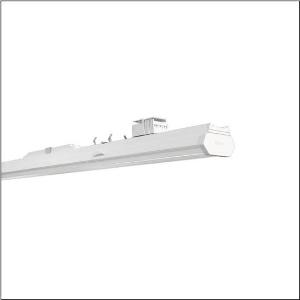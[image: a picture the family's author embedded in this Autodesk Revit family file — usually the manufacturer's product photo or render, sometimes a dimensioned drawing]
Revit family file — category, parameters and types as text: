
# Revit family: licross_r__21_protected_mo_52td1bvn48xg_aeae
name_source: partatom
category: Lighting Fixtures
units: mm (PartAtom-declared; Revit-internal decimal feet)

## family parameters
Cut with Voids When Loaded = No
Host = Face
Light Source = No
Part Type = Normal
Room Calculation Point = No
Round Connector Dimension = Use Diameter
Shared = No

## types (1)
- --- (1 x LED, 8000 lm, 48.3 W, 4000K)
    Apparent Load = 48 VA
    CIE Flux Codes = 54 82 95 97 100
    Color Rendering = 80
    Color Temperature = 4000K
    Default Elevation = 1800 mm
    Description = Licross® 21 Protected MO, luminaire insert, of sheet steel, galvanised, coil coated, white, length: 1.500mm, width: 90mm, height: 101mm, LED rated luminous flux: 8.000lm, light colour: 840, control gear: DALI 2, CLO, with plug, 5-pole, with phase selection, mains connection: 220..240V, AC, 50/60Hz, start of lifetime: 48W, end of service life: 58W, halogen-free wiring, primary optical cover: cover, of PMMA, light emission: direct distribution, primary light characteristic: symmetric, protection rating (complete): IP54, insulation class (complete): insulation class I (protective earthing), certification: CE, ENEC, VDE, UKCA, protection symbol: D if used in an environment with non-conductive dust loads with corresponding accessories, impact resistance: IK06, permissible ambient temperature for indoor applications: -25..+40°C, corresponds to IFS (International Featured Standards) requirements for safety and quality in the food industry, reducing of maximum allowable ambient temperature of 5°C with ceiling mounting, LABS conformity tested according to VDMA 24364:2018-05, packaging unit: 1 piece
    Height = 92 mm
    Lamp = 1 x LED
    Lamp Light Flux = 8000 lm
    Lamp Power = 48.3 W
    Lamp count = 1
    Length = 1500 mm
    Luminous efficacy = 166 lm/W
    Manufacturer = Siteco
    ModVariant = No
    Model = 52TD1BVN48XG
    Mounting Place = Ceiling
    Mounting Type = Pendant
    Number of Poles = 1
    OnlyDefault = Yes
    Power Factor = 1
    Product Name = Licross® 21 Protected MO
    Product group = luminaire insert
    ProductGroupID = 901
    Protection Class = Protection class I
    Protection Degree = IP 54
    RLX_Detail_Level = 1
    RLX_Emergency_Light_Flux = 0 lm
    RLX_Emergency_Type = 0
    RLX_Emergency_Type_DB = No
    RlxData = <blob elided: 24309 chars, md5=22b66ea0>
    Socket = socket
    Standby Power = 0 W
    System Light Flux = 8000 lm
    System Power = 48 W
    Type Comments = factory setting: luminous flux: 100 % | dim-lin: 254 | 326 mA
    Type Image = l_1256148.jpg
    URL = http://relux.com
    VarID = @adj_035215
    Voltage = 0 V
    Weight = 0.00 kg
    Width = 88 mm

## geometry (parser evidence)
native form markers: Blend x4, Sweep x9
no freeform markers — native parametric forms only
